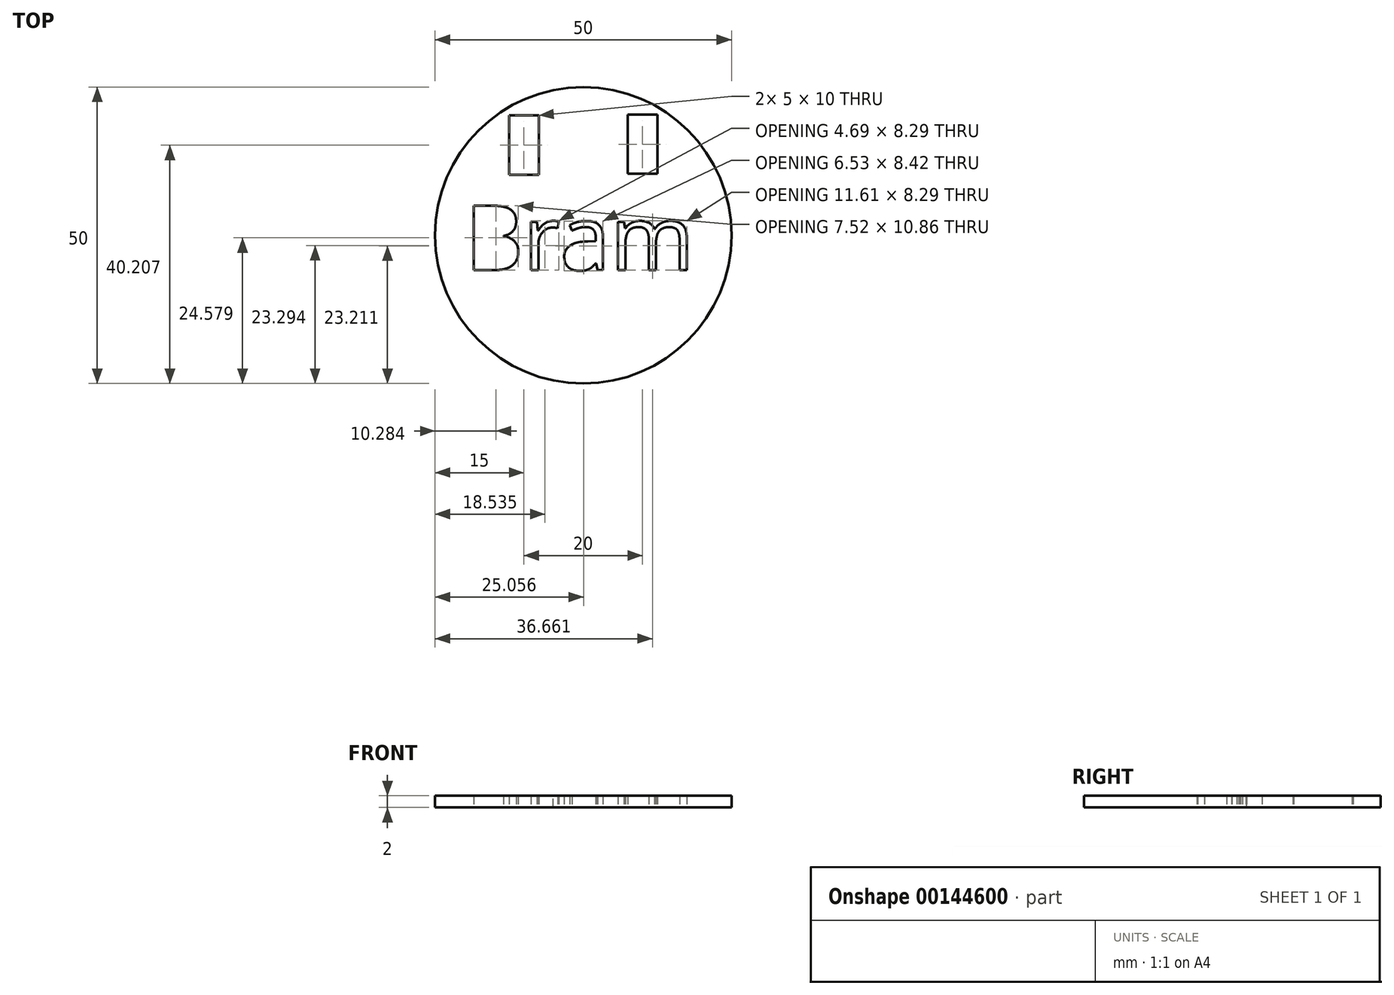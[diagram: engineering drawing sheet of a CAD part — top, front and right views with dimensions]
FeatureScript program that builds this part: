
annotation { "Feature Type Name" : "Feature", "Feature Type Description" : "" }
export const myFeature = defineFeature(function(context is Context, id is Id, definition is map)
    precondition{}
    {
        {
            var Q0;
            Q0=qCreatedBy(makeId("Top.planeOp"),FACE);
            var sketch = newSketch(context, id + "F0", { "sketchPlane" : qUnion([Q0])});
            skCircle(sketch, "E0", {"center": v(0, 0) * mm, "radius": 25 * mm});
            skText(sketch, "E1", { "text": "Bram", "fontName": "OpenSans-Regular.ttf"});
            skLineSegment(sketch, "E2.bottom", {"start": v(-7.5, 20.2) * mm, "end": v(-12.5, 20.2) * mm});
            skLineSegment(sketch, "E2.top", {"start": v(-7.5, 10.2) * mm, "end": v(-12.5, 10.2) * mm});
            skLineSegment(sketch, "E2.left", {"start": v(-7.5, 20.2) * mm, "end": v(-7.5, 10.2) * mm});
            skLineSegment(sketch, "E2.right", {"start": v(-12.5, 20.2) * mm, "end": v(-12.5, 10.2) * mm});
            skLineSegment(sketch, "E3.bottom", {"start": v(12.5, 20.37) * mm, "end": v(7.5, 20.37) * mm});
            skLineSegment(sketch, "E3.top", {"start": v(12.5, 10.37) * mm, "end": v(7.5, 10.37) * mm});
            skLineSegment(sketch, "E3.left", {"start": v(12.5, 20.37) * mm, "end": v(12.5, 10.37) * mm});
            skLineSegment(sketch, "E3.right", {"start": v(7.5, 20.37) * mm, "end": v(7.5, 10.37) * mm});
            const initialGuessF0  = {"E1": [-0.01997, -0.00585, 1, 0, 0.01095]};
            skSetInitialGuess(sketch, initialGuessF0);
            skSolve(sketch);
        }
        {
            var Q0;
            Q0=makeQuery(id+"F0.imprint","IMPRINT",FACE,{"disambiguationData":[TD([[makeQuery(id+"F0.imprint","IMPRINT",EDGE,{"derivedFrom":sQuery(id+"F0.wireOp",EDGE,"E0")}),1.0]])]});
            extrude(context, id + "F1", {"entities" : qUnion([Q0]), "depth" : 2 * mm});
        }
    });
